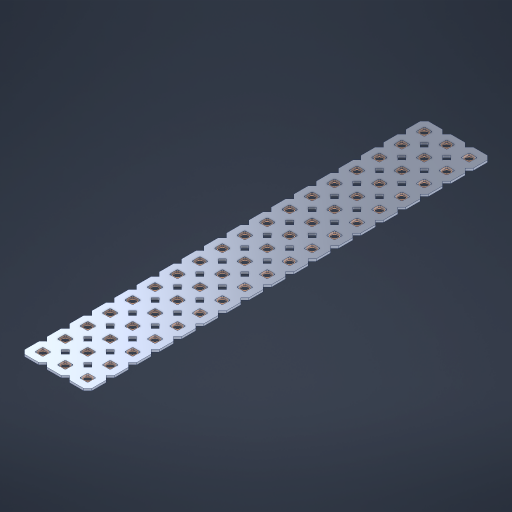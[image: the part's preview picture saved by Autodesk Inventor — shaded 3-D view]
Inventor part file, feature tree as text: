
AUTODESK INVENTOR PART (.ipt)
format: ipt  version: 2023 (Build 270158000, 158)  size: 883,712 bytes
history: native  units: in
note: dims shown in document units (in); Inventor stores cm internally (conversion verified against a paired STEP export)
features: other x55, extrude x53, sketch x2, pattern_linear x1
ambient origin geometry x8: Origin, YZ Plane, XZ Plane, XY Plane, X Axis, Y Axis, Z Axis, Center Point
bodies: Solid1 (feature_tree), Body (feature_tree)
feature tree (111):
  pattern_linear  "Rectangular Pattern1"  Spacing1=0.09in  [1 undecoded]
  sketch  "Sketch1"  dims[d1=0.5in]
  sketch  "Sketch2"  dims[d2=0.182in d3=0.09in d4=0.09in d5=0.09in d6=0.09in d7=0.09in d8=0.09in d9=0.09in d10=0.09in d11=0.02in d13=0.0in d14=0.172in d15=0.0625in d16=0.0in d19=0.5in d22=0.5in]
  other  "Srf1"
  other  "Srf126"
  other  "Srf127"
  other  "Srf128"
  other  "Srf129"
  other  "Srf130"
  other  "Srf131"
  other  "Srf250"
  other  "Srf251"
  other  "Srf252"
  other  "Srf253"
  other  "Srf254"
  other  "Srf255"
  other  "Srf256"
  other  "Srf257"
  other  "Srf258"
  other  "Srf259"
  other  "Srf260"
  other  "Srf268"
  other  "Srf269"
  other  "Srf270"
  other  "Srf271"
  other  "Srf272"
  other  "Srf273"
  other  "Srf274"
  other  "Srf275"
  other  "Srf276"
  other  "Srf277"
  other  "Srf278"
  other  "Srf279"
  other  "Srf280"
  other  "Srf281"
  other  "Srf282"
  other  "Srf283"
  other  "Srf284"
  other  "Srf285"
  other  "Srf293"
  other  "Srf294"
  other  "Srf295"
  other  "Srf296"
  other  "Srf297"
  other  "Srf298"
  other  "Srf299"
  other  "Srf300"
  other  "Srf301"
  other  "Srf302"
  other  "Srf303"
  other  "Srf304"
  other  "Srf305"
  other  "Srf306"
  other  "Srf307"
  other  "Srf308"
  other  "Srf309"
  other  "Srf310"
  other  "Circle"
  extrude  "ExtrusionSrf126"  Depth=0.09in
  extrude  "ExtrusionSrf127"  Depth=0.09in
  extrude  "ExtrusionSrf128"  Depth=0.09in
  extrude  "ExtrusionSrf129"  Depth=0.09in
  extrude  "ExtrusionSrf130"  Depth=0.09in
  extrude  "ExtrusionSrf131"  Depth=0.09in
  extrude  "ExtrusionSrf250"  Depth=0.09in
  extrude  "ExtrusionSrf251"  Depth=0.02in
  extrude  "ExtrusionSrf252"  TaperAngle=0.0deg  [1 undecoded]
  extrude  "ExtrusionSrf253"  Depth=0.5in
  extrude  "ExtrusionSrf254"  Depth=0.5in TaperAngle=0.0deg
  extrude  "ExtrusionSrf255"  Depth=0.5in
  extrude  "ExtrusionSrf256"  Depth=0.5in
  extrude  "ExtrusionSrf257"  [1 undecoded]
  extrude  "ExtrusionSrf258"  [1 undecoded]
  extrude  "ExtrusionSrf259"  [1 undecoded]
  extrude  "ExtrusionSrf260"  [1 undecoded]
  extrude  "ExtrusionSrf268"  [1 undecoded]
  extrude  "ExtrusionSrf269"  [1 undecoded]
  extrude  "ExtrusionSrf270"  [1 undecoded]
  extrude  "ExtrusionSrf271"  [1 undecoded]
  extrude  "ExtrusionSrf272"  [1 undecoded]
  extrude  "ExtrusionSrf273"  [1 undecoded]
  extrude  "ExtrusionSrf274"  [1 undecoded]
  extrude  "ExtrusionSrf275"  [1 undecoded]
  extrude  "ExtrusionSrf276"  [1 undecoded]
  extrude  "ExtrusionSrf277"  [1 undecoded]
  extrude  "ExtrusionSrf278"  [1 undecoded]
  extrude  "ExtrusionSrf279"  [1 undecoded]
  extrude  "ExtrusionSrf280"  [1 undecoded]
  extrude  "ExtrusionSrf281"  [1 undecoded]
  extrude  "ExtrusionSrf282"  [1 undecoded]
  extrude  "ExtrusionSrf283"  [1 undecoded]
  extrude  "ExtrusionSrf284"  [1 undecoded]
  extrude  "ExtrusionSrf285"  [1 undecoded]
  extrude  "ExtrusionSrf293"  [1 undecoded]
  extrude  "ExtrusionSrf294"  [1 undecoded]
  extrude  "ExtrusionSrf295"  [1 undecoded]
  extrude  "ExtrusionSrf296"  [1 undecoded]
  extrude  "ExtrusionSrf297"  [1 undecoded]
  extrude  "ExtrusionSrf298"  [1 undecoded]
  extrude  "ExtrusionSrf299"  [1 undecoded]
  extrude  "ExtrusionSrf300"  [1 undecoded]
  extrude  "ExtrusionSrf301"  [1 undecoded]
  extrude  "ExtrusionSrf302"  [1 undecoded]
  extrude  "ExtrusionSrf303"  [1 undecoded]
  extrude  "ExtrusionSrf304"  [1 undecoded]
  extrude  "ExtrusionSrf305"  [1 undecoded]
  extrude  "ExtrusionSrf306"  [1 undecoded]
  extrude  "ExtrusionSrf307"  [1 undecoded]
  extrude  "ExtrusionSrf308"  [1 undecoded]
  extrude  "ExtrusionSrf309"  [1 undecoded]
  extrude  "ExtrusionSrf310"  [1 undecoded]
note: 42 required parameter values undecoded (feature->parameter linkage not recoverable at this tier; creation-order binding heuristic only, values carry confidence <= 0.55)
